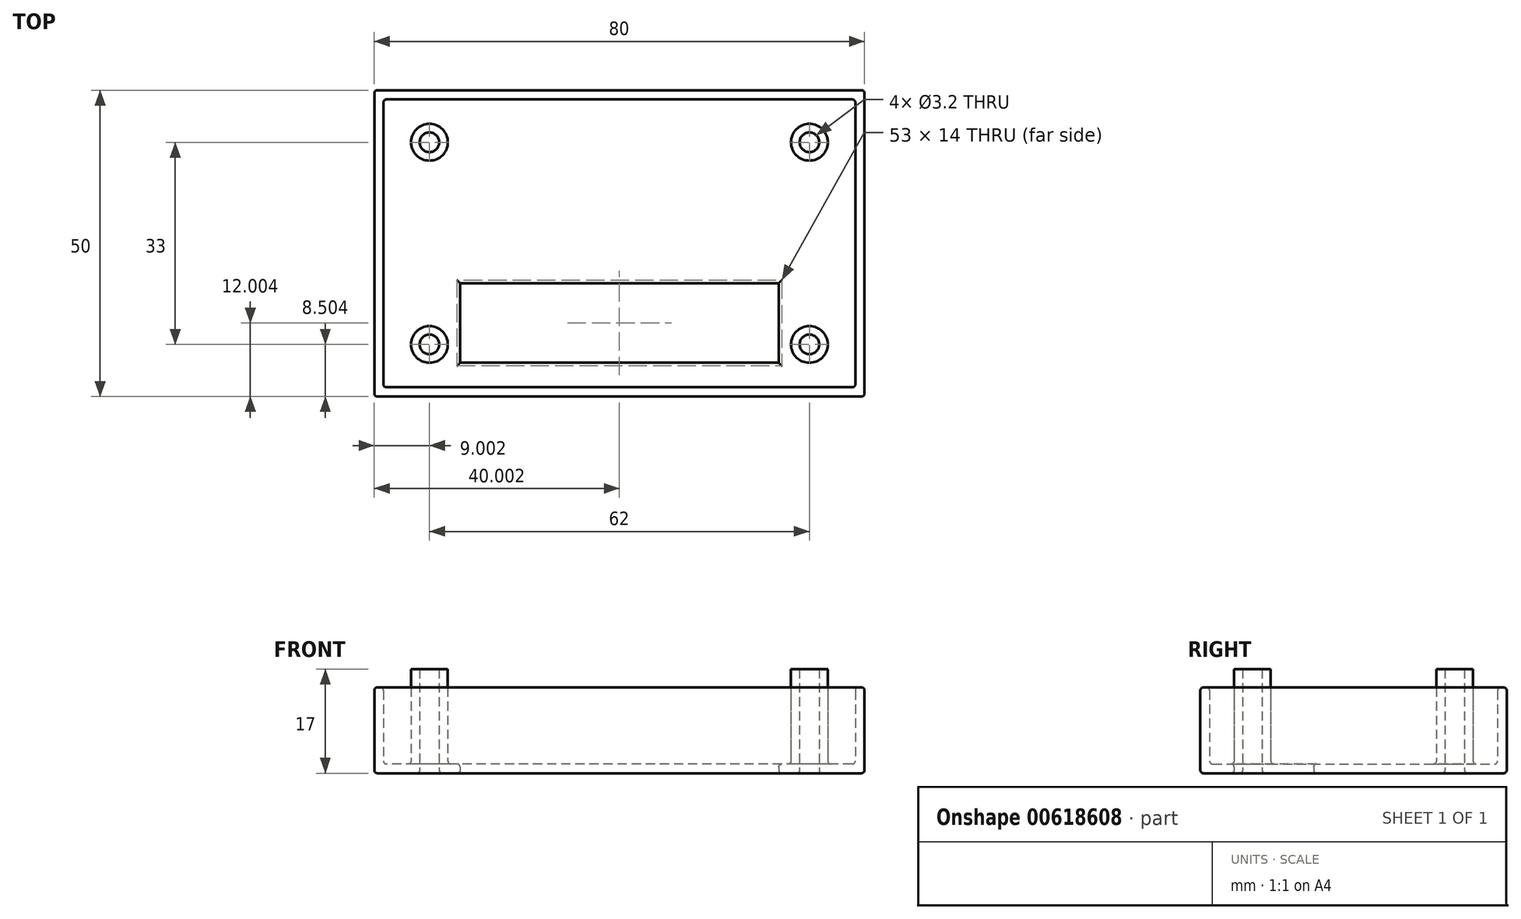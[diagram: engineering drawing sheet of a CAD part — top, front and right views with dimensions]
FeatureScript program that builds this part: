
annotation { "Feature Type Name" : "Feature", "Feature Type Description" : "" }
export const myFeature = defineFeature(function(context is Context, id is Id, definition is map)
    precondition{}
    {
        {
            var Q0;
            Q0=qCreatedBy(makeId("Top.planeOp"),FACE);
            var sketch = newSketch(context, id + "F0", { "sketchPlane" : qUnion([Q0])});
            skLineSegment(sketch, "E0.bottom", {"start": v(-52.19, 52.66) * mm, "end": v(27.81, 52.66) * mm});
            skLineSegment(sketch, "E0.top", {"start": v(-52.19, 2.66) * mm, "end": v(27.81, 2.66) * mm});
            skLineSegment(sketch, "E0.left", {"start": v(-52.19, 52.66) * mm, "end": v(-52.19, 2.66) * mm});
            skLineSegment(sketch, "E0.right", {"start": v(27.81, 52.66) * mm, "end": v(27.81, 2.66) * mm});
            skPoint(sketch, "E1", {"position": v(-43.19, 44.16) * mm});
            skPoint(sketch, "E2", {"position": v(-43.19, 11.16) * mm});
            skPoint(sketch, "E3", {"position": v(18.81, 11.16) * mm});
            skPoint(sketch, "E4", {"position": v(18.81, 44.16) * mm});
            skCircle(sketch, "E5", {"center": v(-43.19, 44.16) * mm, "radius": 3 * mm});
            skCircle(sketch, "E6", {"center": v(-43.19, 11.16) * mm, "radius": 3 * mm});
            skCircle(sketch, "E7", {"center": v(18.81, 11.16) * mm, "radius": 3 * mm});
            skCircle(sketch, "E8", {"center": v(18.81, 44.16) * mm, "radius": 3 * mm});
            skLineSegment(sketch, "E9.bottom", {"start": v(-50.69, 51.16) * mm, "end": v(26.31, 51.16) * mm});
            skLineSegment(sketch, "E9.top", {"start": v(-50.69, 4.16) * mm, "end": v(26.31, 4.16) * mm});
            skLineSegment(sketch, "E9.left", {"start": v(-50.69, 51.16) * mm, "end": v(-50.69, 4.16) * mm});
            skLineSegment(sketch, "E9.right", {"start": v(26.31, 51.16) * mm, "end": v(26.31, 4.16) * mm});
            skLineSegment(sketch, "E10.bottom", {"start": v(13.81, 21.16) * mm, "end": v(-38.19, 21.16) * mm});
            skLineSegment(sketch, "E10.top", {"start": v(13.81, 8.16) * mm, "end": v(-38.19, 8.16) * mm});
            skLineSegment(sketch, "E10.left", {"start": v(13.81, 21.16) * mm, "end": v(13.81, 8.16) * mm});
            skLineSegment(sketch, "E10.right", {"start": v(-38.19, 21.16) * mm, "end": v(-38.19, 8.16) * mm});
            skSolve(sketch);
        }
        {
            var Q0;
            Q0=qSketchRegion(id+"F0",true);
            var Q1;
            Q1=makeQuery(id+"F0.imprint","IMPRINT",FACE,{"disambiguationData":[TD([[makeQuery(id+"F0.imprint","IMPRINT",EDGE,{"derivedFrom":sQuery(id+"F0.wireOp",EDGE,"E5")}),-1.0]])]});
            var Q2;
            Q2=makeQuery(id+"F0.imprint","IMPRINT",FACE,{"disambiguationData":[TD([[makeQuery(id+"F0.imprint","IMPRINT",EDGE,{"derivedFrom":sQuery(id+"F0.wireOp",EDGE,"E7")}),1.0]])]});
            var Q3;
            Q3=makeQuery(id+"F0.imprint","IMPRINT",FACE,{"disambiguationData":[TD([[makeQuery(id+"F0.imprint","IMPRINT",EDGE,{"derivedFrom":sQuery(id+"F0.wireOp",EDGE,"E6")}),1.0]])]});
            var Q4;
            Q4=makeQuery(id+"F0.imprint","IMPRINT",FACE,{"disambiguationData":[TD([[makeQuery(id+"F0.imprint","IMPRINT",EDGE,{"derivedFrom":sQuery(id+"F0.wireOp",EDGE,"E5")}),1.0]])]});
            var Q5;
            Q5=makeQuery(id+"F0.imprint","IMPRINT",FACE,{"disambiguationData":[TD([[makeQuery(id+"F0.imprint","IMPRINT",EDGE,{"derivedFrom":sQuery(id+"F0.wireOp",EDGE,"E8")}),1.0]])]});
            extrude(context, id + "F1", {"entities" : qUnion([Q0, Q1, Q2, Q3, Q4, Q5]), "depth" : 1.5 * mm, "offsetDistance" : 25 * mm});
        }
        {
            var Q0;
            Q0=makeQuery(id+"F0.imprint","IMPRINT",FACE,{"disambiguationData":[TD([[makeQuery(id+"F0.imprint","IMPRINT",EDGE,{"derivedFrom":sQuery(id+"F0.wireOp",EDGE,"E0.bottom")}),-1.0]])]});
            extrude(context, id + "F2", {"entities" : qUnion([Q0]), "operationType" : NewBodyOperationType.ADD, "depth" : 14 * mm, "offsetDistance" : 25 * mm});
        }
        {
            var Q0;
            Q0=makeQuery(id+"F0.imprint","IMPRINT",FACE,{"disambiguationData":[TD([[makeQuery(id+"F0.imprint","IMPRINT",EDGE,{"derivedFrom":sQuery(id+"F0.wireOp",EDGE,"E5")}),1.0]])]});
            var Q1;
            Q1=makeQuery(id+"F0.imprint","IMPRINT",FACE,{"disambiguationData":[TD([[makeQuery(id+"F0.imprint","IMPRINT",EDGE,{"derivedFrom":sQuery(id+"F0.wireOp",EDGE,"E6")}),1.0]])]});
            var Q2;
            Q2=makeQuery(id+"F0.imprint","IMPRINT",FACE,{"disambiguationData":[TD([[makeQuery(id+"F0.imprint","IMPRINT",EDGE,{"derivedFrom":sQuery(id+"F0.wireOp",EDGE,"E8")}),1.0]])]});
            var Q3;
            Q3=makeQuery(id+"F0.imprint","IMPRINT",FACE,{"disambiguationData":[TD([[makeQuery(id+"F0.imprint","IMPRINT",EDGE,{"derivedFrom":sQuery(id+"F0.wireOp",EDGE,"E7")}),1.0]])]});
            extrude(context, id + "F3", {"entities" : qUnion([Q0, Q1, Q2, Q3]), "operationType" : NewBodyOperationType.ADD, "depth" : 17 * mm, "offsetDistance" : 25 * mm});
        }
        {
            var Q0;
            Q0=sQuery(id+"F0.wireOp",VERTEX,"E3");
            var Q1;
            Q1=sQuery(id+"F0.wireOp",VERTEX,"E2");
            var Q2;
            Q2=sQuery(id+"F0.wireOp",VERTEX,"E1");
            var Q3;
            Q3=sQuery(id+"F0.wireOp",VERTEX,"E4");
            var Q4;
            Q4=makeQuery(id+"F1.opExtrude","SWEPT_BODY",BODY,{"disambiguationData":[OSD([sQuery(id+"F0.wireOp",EDGE,"E0.bottom"),sQuery(id+"F0.wireOp",EDGE,"E0.top"),sQuery(id+"F0.wireOp",EDGE,"E0.left"),sQuery(id+"F0.wireOp",EDGE,"E0.right")])]});
            hole(context, id + "F4", {"style" : HoleStyle.SIMPLE, "endStyle" : HoleEndStyle.THROUGH, "oppositeDirection" : true, "holeDiameter" : 3.2 * mm, "majorDiameter" : 5 * mm, "isTappedThrough" : true, "tappedDepth" : 12 * mm, "tapClearance" : 3, "locations" : qUnion([Q0, Q1, Q2, Q3]), "scope" : qUnion([Q4])});
        }
        {
            var Q0;
            Q0=makeQuery(id+"F1.opExtrude","CAP_FACE",FACE,{"disambiguationData":[OSD([sQuery(id+"F0.wireOp",EDGE,"E0.bottom"),sQuery(id+"F0.wireOp",EDGE,"E0.top"),sQuery(id+"F0.wireOp",EDGE,"E0.left"),sQuery(id+"F0.wireOp",EDGE,"E0.right"),sQuery(id+"F0.wireOp",EDGE,"E10.bottom"),sQuery(id+"F0.wireOp",EDGE,"E10.top"),sQuery(id+"F0.wireOp",EDGE,"E10.left"),sQuery(id+"F0.wireOp",EDGE,"E10.right")])],"isStart":true});
            var Q1;
            {var subQ0=sQuery(id+"F0.wireOp",EDGE,"E0.right");var subQ1=sQuery(id+"F0.wireOp",EDGE,"E0.bottom");Q1=makeQuery(id+"F2.boolean.opBoolean","MERGE",EDGE,{"derivedFrom":[makeQuery(id+"F1.opExtrude","SWEPT_EDGE",EDGE,{"disambiguationData":[OSD([subQ1,subQ0])]}),makeQuery(id+"F2.opExtrude","SWEPT_EDGE",EDGE,{"disambiguationData":[OSD([subQ1,subQ0])]})]});}
            var Q2;
            {var subQ0=sQuery(id+"F0.wireOp",EDGE,"E0.left");var subQ1=sQuery(id+"F0.wireOp",EDGE,"E0.bottom");Q2=makeQuery(id+"F2.boolean.opBoolean","MERGE",EDGE,{"derivedFrom":[makeQuery(id+"F1.opExtrude","SWEPT_EDGE",EDGE,{"disambiguationData":[OSD([subQ1,subQ0])]}),makeQuery(id+"F2.opExtrude","SWEPT_EDGE",EDGE,{"disambiguationData":[OSD([subQ1,subQ0])]})]});}
            var Q3;
            {var subQ0=sQuery(id+"F0.wireOp",EDGE,"E0.left");var subQ1=sQuery(id+"F0.wireOp",EDGE,"E0.top");Q3=makeQuery(id+"F2.boolean.opBoolean","MERGE",EDGE,{"derivedFrom":[makeQuery(id+"F1.opExtrude","SWEPT_EDGE",EDGE,{"disambiguationData":[OSD([subQ1,subQ0])]}),makeQuery(id+"F2.opExtrude","SWEPT_EDGE",EDGE,{"disambiguationData":[OSD([subQ1,subQ0])]})]});}
            var Q4;
            Q4=makeQuery(id+"F2.opExtrude","CAP_EDGE",EDGE,{"disambiguationData":[OSD([sQuery(id+"F0.wireOp",EDGE,"E0.top")])],"isStart":false});
            var Q5;
            Q5=makeQuery(id+"F2.opExtrude","CAP_EDGE",EDGE,{"disambiguationData":[OSD([sQuery(id+"F0.wireOp",EDGE,"E0.left")])],"isStart":false});
            var Q6;
            {var subQ0=sQuery(id+"F0.wireOp",EDGE,"E0.right");var subQ1=sQuery(id+"F0.wireOp",EDGE,"E0.top");Q6=makeQuery(id+"F2.boolean.opBoolean","MERGE",EDGE,{"derivedFrom":[makeQuery(id+"F1.opExtrude","SWEPT_EDGE",EDGE,{"disambiguationData":[OSD([subQ1,subQ0])]}),makeQuery(id+"F2.opExtrude","SWEPT_EDGE",EDGE,{"disambiguationData":[OSD([subQ1,subQ0])]})]});}
            var Q7;
            Q7=makeQuery(id+"F2.opExtrude","CAP_EDGE",EDGE,{"disambiguationData":[OSD([sQuery(id+"F0.wireOp",EDGE,"E0.right")])],"isStart":false});
            var Q8;
            Q8=makeQuery(id+"F1.opExtrude","CAP_FACE",FACE,{"disambiguationData":[OSD([sQuery(id+"F0.wireOp",EDGE,"E0.bottom"),sQuery(id+"F0.wireOp",EDGE,"E0.top"),sQuery(id+"F0.wireOp",EDGE,"E0.left"),sQuery(id+"F0.wireOp",EDGE,"E0.right"),sQuery(id+"F0.wireOp",EDGE,"E10.bottom"),sQuery(id+"F0.wireOp",EDGE,"E10.top"),sQuery(id+"F0.wireOp",EDGE,"E10.left"),sQuery(id+"F0.wireOp",EDGE,"E10.right")])],"isStart":false});
            var Q9;
            Q9=makeQuery(id+"F2.opExtrude","SWEPT_EDGE",EDGE,{"disambiguationData":[OSD([sQuery(id+"F0.wireOp",EDGE,"E9.top"),sQuery(id+"F0.wireOp",EDGE,"E9.right")])]});
            var Q10;
            Q10=makeQuery(id+"F2.opExtrude","CAP_EDGE",EDGE,{"disambiguationData":[OSD([sQuery(id+"F0.wireOp",EDGE,"E9.top")])],"isStart":false});
            var Q11;
            Q11=makeQuery(id+"F2.opExtrude","CAP_EDGE",EDGE,{"disambiguationData":[OSD([sQuery(id+"F0.wireOp",EDGE,"E9.right")])],"isStart":false});
            var Q12;
            Q12=makeQuery(id+"F2.opExtrude","CAP_EDGE",EDGE,{"disambiguationData":[OSD([sQuery(id+"F0.wireOp",EDGE,"E9.bottom")])],"isStart":false});
            var Q13;
            Q13=makeQuery(id+"F2.opExtrude","CAP_EDGE",EDGE,{"disambiguationData":[OSD([sQuery(id+"F0.wireOp",EDGE,"E0.bottom")])],"isStart":false});
            var Q14;
            {var subQ0=sQuery(id+"F0.wireOp",EDGE,"E0.left");Q14=makeQuery(id+"F2.boolean.opBoolean","MERGE",FACE,{"derivedFrom":[makeQuery(id+"F1.opExtrude","SWEPT_FACE",FACE,{"disambiguationData":[OSD([subQ0])]}),makeQuery(id+"F2.opExtrude","SWEPT_FACE",FACE,{"disambiguationData":[OSD([subQ0])]})]});}
            var Q15;
            Q15=makeQuery(id+"F2.opExtrude","CAP_EDGE",EDGE,{"disambiguationData":[OSD([sQuery(id+"F0.wireOp",EDGE,"E9.left")])],"isStart":false});
            var Q16;
            Q16=makeQuery(id+"F2.opExtrude","SWEPT_EDGE",EDGE,{"disambiguationData":[OSD([sQuery(id+"F0.wireOp",EDGE,"E9.bottom"),sQuery(id+"F0.wireOp",EDGE,"E9.right")])]});
            var Q17;
            Q17=makeQuery(id+"F2.opExtrude","SWEPT_EDGE",EDGE,{"disambiguationData":[OSD([sQuery(id+"F0.wireOp",EDGE,"E9.bottom"),sQuery(id+"F0.wireOp",EDGE,"E9.left")])]});
            var Q18;
            Q18=makeQuery(id+"F2.opExtrude","SWEPT_EDGE",EDGE,{"disambiguationData":[OSD([sQuery(id+"F0.wireOp",EDGE,"E9.top"),sQuery(id+"F0.wireOp",EDGE,"E9.left")])]});
            fillet(context, id + "F5", {"entities" : qUnion([Q0, Q1, Q2, Q3, Q4, Q5, Q6, Q7, Q8, Q9, Q10, Q11, Q12, Q13, Q14, Q15, Q16, Q17, Q18]), "radius" : .5 * mm, "tangentPropagation" : true, "allowEdgeOverflow" : false});
        }
    });
